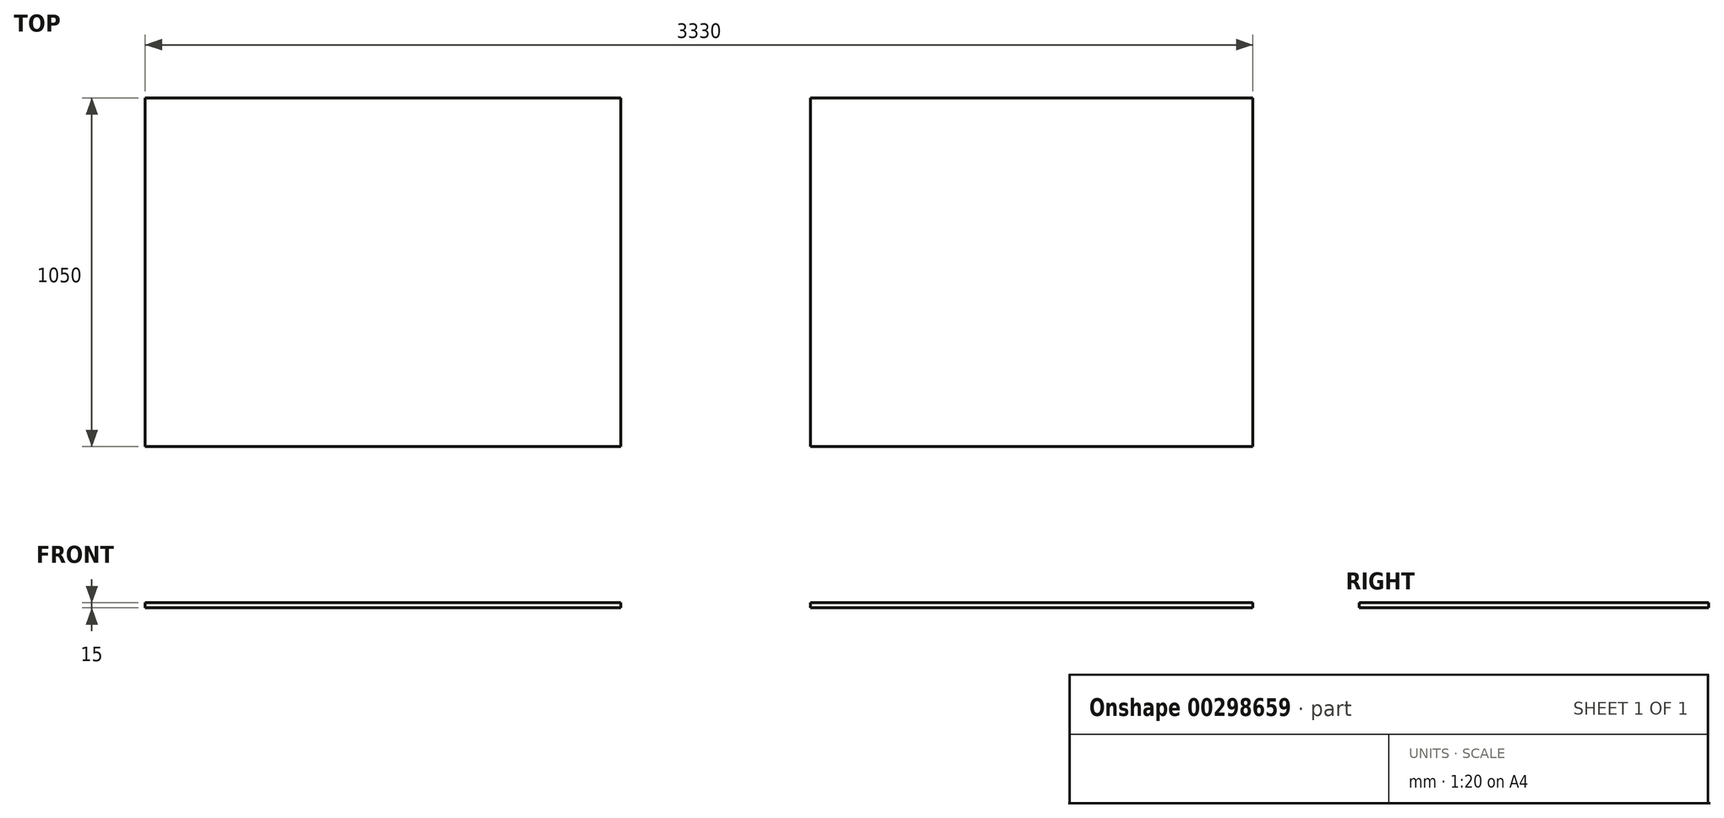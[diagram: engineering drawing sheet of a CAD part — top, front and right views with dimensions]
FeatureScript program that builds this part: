
annotation { "Feature Type Name" : "Feature", "Feature Type Description" : "" }
export const myFeature = defineFeature(function(context is Context, id is Id, definition is map)
    precondition{}
    {
        {
            var Q0;
            Q0=qCreatedBy(makeId("Top.planeOp"),FACE);
            var sketch = newSketch(context, id + "F0", { "sketchPlane" : qUnion([Q0])});
            skLineSegment(sketch, "E0.bottom", {"start": v(0, 0) * mm, "end": v(1430, 0) * mm});
            skLineSegment(sketch, "E0.top", {"start": v(0, 1050) * mm, "end": v(1430, 1050) * mm});
            skLineSegment(sketch, "E0.left", {"start": v(0, 0) * mm, "end": v(0, 1050) * mm});
            skLineSegment(sketch, "E0.right", {"start": v(1430, 0) * mm, "end": v(1430, 1050) * mm});
            skSolve(sketch);
        }
        {
            var Q0;
            Q0 = qSketchRegion(id + "F0", true);
            extrude(context, id + "F1", {"entities" : qUnion([Q0]), "depth" : 15 * mm});
        }
        {
            var Q0;
            Q0=makeQuery(id+"F1.opExtrude","SWEPT_BODY",BODY,{"disambiguationData":[OSD([sQuery(id+"F0.wireOp",EDGE,"E0.bottom"),sQuery(id+"F0.wireOp",EDGE,"E0.top"),sQuery(id+"F0.wireOp",EDGE,"E0.left"),sQuery(id+"F0.wireOp",EDGE,"E0.right")])]});
            transform(context, id + "F2", {"entities" : qUnion([Q0]), "transformType" : TransformType.TRANSLATION_3D, "dx" : 2000 * mm, "dy" : 0 * mm, "dz" : 0 * mm, "makeCopy" : true});
        }
        {
            var Q0;
            Q0=makeQuery(id+"F2.opPattern","COPY",FACE,{"derivedFrom":makeQuery(id+"F1.opExtrude","CAP_FACE",FACE,{"disambiguationData":[OSD([sQuery(id+"F0.wireOp",EDGE,"E0.bottom"),sQuery(id+"F0.wireOp",EDGE,"E0.top"),sQuery(id+"F0.wireOp",EDGE,"E0.left"),sQuery(id+"F0.wireOp",EDGE,"E0.right")])],"isStart":false}),"instanceName":"1"});
            var sketch = newSketch(context, id + "F3", { "sketchPlane" : qUnion([Q0])});
            skLineSegment(sketch, "E1", {"start": v(2000, 525) * mm, "end": v(3430, 525) * mm, "construction": true});
            skLineSegment(sketch, "E2.bottom", {"start": v(3500, 675) * mm, "end": v(3800, 675) * mm});
            skLineSegment(sketch, "E2.top", {"start": v(3500, 375) * mm, "end": v(3800, 375) * mm});
            skLineSegment(sketch, "E2.left", {"start": v(3500, 675) * mm, "end": v(3500, 375) * mm});
            skLineSegment(sketch, "E2.right", {"start": v(3800, 675) * mm, "end": v(3800, 375) * mm});
            skLineSegment(sketch, "E3.bottom", {"start": v(3430, 1050) * mm, "end": v(3330, 1050) * mm});
            skLineSegment(sketch, "E3.top", {"start": v(3430, 0) * mm, "end": v(3330, 0) * mm});
            skLineSegment(sketch, "E3.left", {"start": v(3430, 1050) * mm, "end": v(3430, 0) * mm});
            skLineSegment(sketch, "E3.right", {"start": v(3330, 1050) * mm, "end": v(3330, 0) * mm});
            skSolve(sketch);
        }
        {
            var Q0;
            Q0 = qSketchRegion(id + "F3", true);
            extrude(context, id + "F4", {"entities" : qUnion([Q0]), "operationType" : NewBodyOperationType.REMOVE, "endBound" : BoundingType.THROUGH_ALL, "oppositeDirection" : true, "depth" : 25 * mm});
        }
    });
